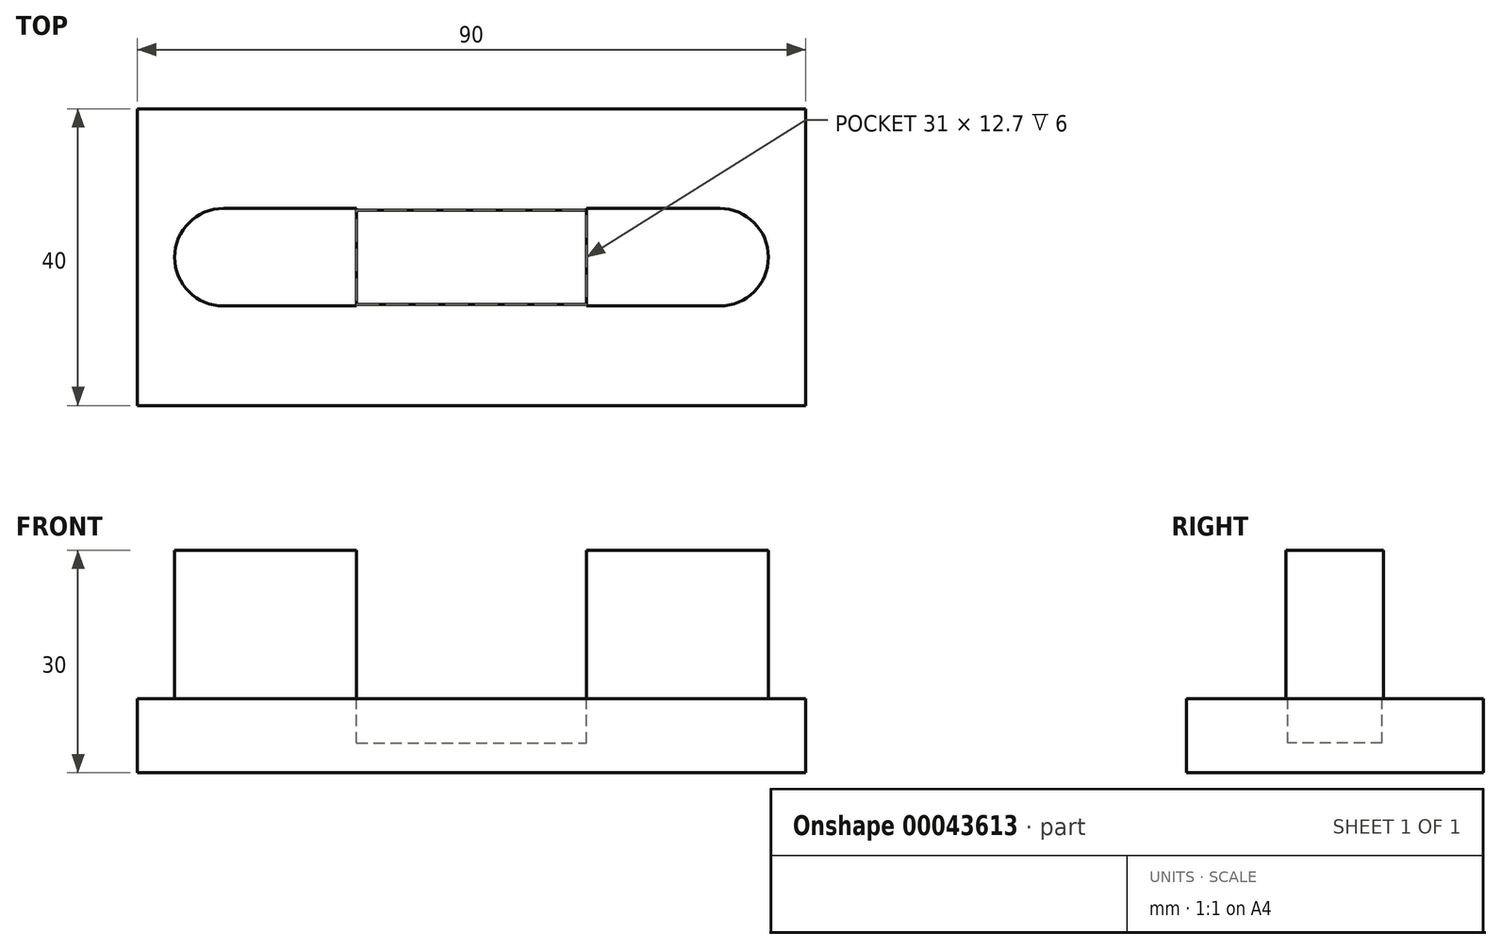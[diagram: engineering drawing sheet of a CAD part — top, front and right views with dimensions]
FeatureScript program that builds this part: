
annotation { "Feature Type Name" : "Feature", "Feature Type Description" : "" }
export const myFeature = defineFeature(function(context is Context, id is Id, definition is map)
    precondition{}
    {
        {
            var Q0;
            Q0=qCreatedBy(makeId("Front.planeOp"),FACE);
            var sketch = newSketch(context, id + "F0", { "sketchPlane" : qUnion([Q0])});
            skLineSegment(sketch, "E0.bottom", {"start": v(-40.55, 8.73) * mm, "end": v(49.45, 8.73) * mm});
            skLineSegment(sketch, "E0.top", {"start": v(-40.55, -31.27) * mm, "end": v(49.45, -31.27) * mm});
            skLineSegment(sketch, "E0.left", {"start": v(-40.55, 8.73) * mm, "end": v(-40.55, -31.27) * mm});
            skLineSegment(sketch, "E0.right", {"start": v(49.45, 8.73) * mm, "end": v(49.45, -31.27) * mm});
            skLineSegment(sketch, "E1", {"start": v(-40.55, -31.27) * mm, "end": v(49.45, 8.73) * mm, "construction": true});
            skLineSegment(sketch, "E2", {"start": v(49.45, -31.27) * mm, "end": v(4.45, -11.27) * mm, "construction": true});
            skLineSegment(sketch, "E3", {"start": v(4.45, -11.27) * mm, "end": v(-40.55, 8.73) * mm, "construction": true});
            skSolve(sketch);
        }
        {
            var Q0;
            Q0=makeQuery(id+"F0.imprint","IMPRINT",FACE,{"disambiguationData":[TD([[makeQuery(id+"F0.imprint","IMPRINT",EDGE,{"derivedFrom":sQuery(id+"F0.wireOp",EDGE,"E0.bottom")}),-1.0]])]});
            extrude(context, id + "F1", {"entities" : qUnion([Q0]), "depth" : 10 * mm});
        }
        {
            var Q0;
            Q0=makeQuery(id+"F1.opExtrude","CAP_FACE",FACE,{"disambiguationData":[OSD([sQuery(id+"F0.wireOp",EDGE,"E0.bottom"),sQuery(id+"F0.wireOp",EDGE,"E0.top"),sQuery(id+"F0.wireOp",EDGE,"E0.left"),sQuery(id+"F0.wireOp",EDGE,"E0.right")])],"isStart":false});
            var sketch = newSketch(context, id + "F2", { "sketchPlane" : qUnion([Q0])});
            skLineSegment(sketch, "E4.bottom", {"start": v(-11.05, -4.92) * mm, "end": v(19.95, -4.92) * mm});
            skLineSegment(sketch, "E4.top", {"start": v(-11.05, -17.62) * mm, "end": v(19.95, -17.62) * mm});
            skLineSegment(sketch, "E4.left", {"start": v(-11.05, -4.92) * mm, "end": v(-11.05, -17.62) * mm});
            skLineSegment(sketch, "E4.right", {"start": v(19.95, -4.92) * mm, "end": v(19.95, -17.62) * mm});
            skLineSegment(sketch, "E5", {"start": v(19.95, -4.92) * mm, "end": v(49.45, 8.73) * mm, "construction": true});
            skLineSegment(sketch, "E6", {"start": v(19.95, -17.62) * mm, "end": v(49.45, -31.27) * mm, "construction": true});
            skLineSegment(sketch, "E7", {"start": v(-11.05, -17.62) * mm, "end": v(-40.55, -31.27) * mm, "construction": true});
            skSolve(sketch);
        }
        {
            var Q0;
            Q0 = qSketchRegion(id + "F2", true);
            extrude(context, id + "F3", {"entities" : qUnion([Q0]), "operationType" : NewBodyOperationType.REMOVE, "oppositeDirection" : true, "depth" : 6 * mm});
        }
        {
            var Q0;
            Q0=makeQuery(id+"F1.opExtrude","CAP_FACE",FACE,{"disambiguationData":[OSD([sQuery(id+"F0.wireOp",EDGE,"E0.bottom"),sQuery(id+"F0.wireOp",EDGE,"E0.top"),sQuery(id+"F0.wireOp",EDGE,"E0.left"),sQuery(id+"F0.wireOp",EDGE,"E0.right")])],"isStart":false});
            var sketch = newSketch(context, id + "F4", { "sketchPlane" : qUnion([Q0])});
            skLineSegment(sketch, "E8.top", {"start": v(-11.05, -17.84) * mm, "end": v(-28.97, -17.84) * mm});
            skLineSegment(sketch, "E8.left", {"start": v(-11.05, -4.7) * mm, "end": v(-11.05, -17.84) * mm});
            skArc(sketch, "E9", {"start": v(-28.97, -4.7) * mm, "mid": v(-35.55, -11.27) * mm, "end": v(-28.97, -17.84) * mm});
            skLineSegment(sketch, "E10", {"start": v(-28.97, -11.27) * mm, "end": v(-11.05, -11.27) * mm, "construction": true});
            skPoint(sketch, "E10.endSnap0", {"position": v(19.4, -11.27) * mm});
            skLineSegment(sketch, "E11", {"start": v(-28.97, -4.7) * mm, "end": v(-11.05, -4.7) * mm});
            skLineSegment(sketch, "E12", {"start": v(4.45, -4.92) * mm, "end": v(4.45, -24.75) * mm, "construction": true});
            skLineSegment(sketch, "E13.MirrorCS", {"start": v(37.88, -4.7) * mm, "end": v(19.95, -4.7) * mm});
            skLineSegment(sketch, "E14.MirrorCS", {"start": v(19.95, -4.7) * mm, "end": v(19.95, -17.84) * mm});
            skLineSegment(sketch, "E15.MirrorCS", {"start": v(37.88, -11.27) * mm, "end": v(19.95, -11.27) * mm, "construction": true});
            skLineSegment(sketch, "E16.MirrorCS", {"start": v(19.95, -17.84) * mm, "end": v(37.88, -17.84) * mm});
            skArc(sketch, "E17.MirrorCS", {"start": v(37.88, -4.7) * mm, "mid": v(44.45, -11.27) * mm, "end": v(37.88, -17.84) * mm});
            skLineSegment(sketch, "E18", {"start": v(-35.55, -11.27) * mm, "end": v(-35.55, 8.42) * mm, "construction": true});
            skLineSegment(sketch, "E19", {"start": v(44.45, 8.42) * mm, "end": v(44.45, -11.27) * mm, "construction": true});
            skSolve(sketch);
        }
        {
            var Q0;
            {var subQ1=sQuery(id+"F4.wireOp",EDGE,"E13.MirrorCS");Q0=makeQuery(id+"F4.imprint","IMPRINT",FACE,{"disambiguationData":[TD([[makeQuery(id+"F4.imprint","IMPRINT",EDGE,{"derivedFrom":subQ1}),1.0]])]});}
            var Q1;
            {var subQ1=sQuery(id+"F4.wireOp",EDGE,"E8.top");Q1=makeQuery(id+"F4.imprint","IMPRINT",FACE,{"disambiguationData":[TD([[makeQuery(id+"F4.imprint","IMPRINT",EDGE,{"derivedFrom":subQ1}),-1.0]])]});}
            extrude(context, id + "F5", {"entities" : qUnion([Q0, Q1]), "operationType" : NewBodyOperationType.ADD, "depth" : 20 * mm});
        }
        {
            var Q0;
            Q0=makeQuery(id+"F1.opExtrude","SWEPT_BODY",BODY,{"disambiguationData":[OSD([sQuery(id+"F0.wireOp",EDGE,"E0.bottom"),sQuery(id+"F0.wireOp",EDGE,"E0.top"),sQuery(id+"F0.wireOp",EDGE,"E0.left"),sQuery(id+"F0.wireOp",EDGE,"E0.right")])]});
            var Q1;
            Q1=makeQuery(id+"F1.opExtrude","CAP_EDGE",EDGE,{"disambiguationData":[OSD([sQuery(id+"F0.wireOp",EDGE,"E0.bottom")])],"isStart":true});
            transform(context, id + "F6", {"entities" : qUnion([Q0]), "transformType" : TransformType.ROTATION, "transformAxis" : qUnion([Q1]), "angle" : 270 * degree, "makeCopy" : false});
        }
    });
